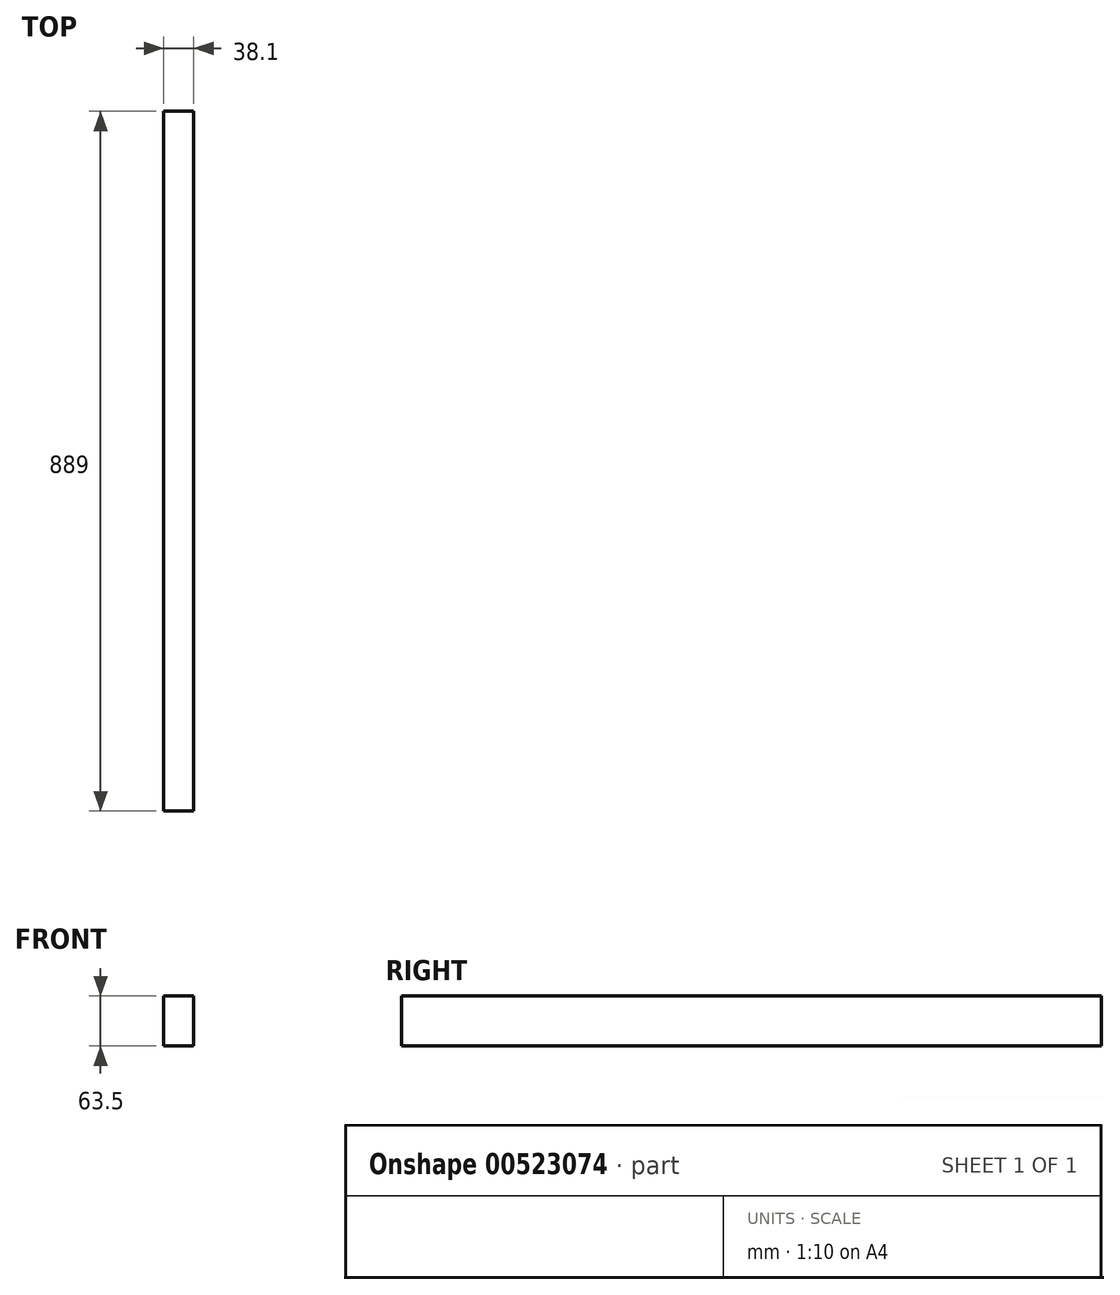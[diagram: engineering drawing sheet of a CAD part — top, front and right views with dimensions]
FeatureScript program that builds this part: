
annotation { "Feature Type Name" : "Feature", "Feature Type Description" : "" }
export const myFeature = defineFeature(function(context is Context, id is Id, definition is map)
    precondition{}
    {
        {
            var Q0;
            Q0=qCreatedBy(makeId("Front.planeOp"),FACE);
            var sketch = newSketch(context, id + "F0", { "sketchPlane" : qUnion([Q0])});
            skLineSegment(sketch, "E0.bottom", {"start": v(0, 0) * mm, "end": v(38.1, 0) * mm});
            skLineSegment(sketch, "E0.top", {"start": v(0, 63.5) * mm, "end": v(38.1, 63.5) * mm});
            skLineSegment(sketch, "E0.left", {"start": v(0, 0) * mm, "end": v(0, 63.5) * mm});
            skLineSegment(sketch, "E0.right", {"start": v(38.1, 0) * mm, "end": v(38.1, 63.5) * mm});
            skSolve(sketch);
        }
        {
            var Q0;
            Q0 = qSketchRegion(id + "F0", true);
            extrude(context, id + "F1", {"entities" : qUnion([Q0]), "depth" : 889 * mm, "offsetDistance" : 25.4 * mm});
        }
    });
